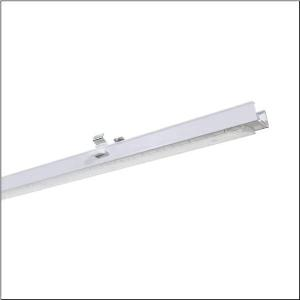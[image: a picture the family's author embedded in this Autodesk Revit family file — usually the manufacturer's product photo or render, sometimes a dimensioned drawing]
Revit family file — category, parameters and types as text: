
# Revit family: trunking_flex_31_51re14mb4cb
name_source: partatom
category: Lighting Fixtures
units: mm (PartAtom-declared; Revit-internal decimal feet)

## family parameters
Cut with Voids When Loaded = No
Host = Face
Light Source = No
Part Type = Normal
Room Calculation Point = No
Round Connector Dimension = Use Diameter
Shared = No

## types (1)
- --- (1 x LED, 11500 lm, 66 W, 4000K)
    Apparent Load = 66 VA
    CIE Flux Codes = 72 92 98 99 100
    Color Rendering = 80
    Color Temperature = 4000K
    Default Elevation = 1800 mm
    Description = Trunking Flex 31, luminaire insert, of extruded aluminium section, coated, traffic white (RAL 9016), length: 1.472mm, width: 91mm, height: 53mm, LED rated luminous flux: 11.500lm, light colour: 840, control gear: ON/OFF Multilumen, with system connector: socket, mains connection: 220..240V, AC, 50/60Hz, rated input power: 66W, connected load according to luminous flux setting (19/24/32/37/47/52/60/66W), luminous flux adjustable on luminaire in eight steps (3450/4380/5800/6700/8350/9200/10500/11500lm ), primary light control with lens, of plastic, primary optical cover: cover, of PMMA, light emission: direct distribution, primary light characteristic: asymmetric, protection rating (complete): IP20, insulation class (complete): insulation class I (protective earthing), certification: CE, UKCA, impact resistance: IK02, permissible ambient temperature for indoor applications: -20..+40°C, packaging unit: 1 piece
    Height = 58 mm
    Lamp = 1 x LED
    Lamp Light Flux = 11500 lm
    Lamp Power = 66 W
    Lamp count = 1
    Length = 1472 mm
    Luminous efficacy = 174 lm/W
    Manufacturer = Siteco
    ModVariant = No
    Model = 51RE14MB4CB
    Mounting Place = Ceiling
    Mounting Type = Pendant
    Number of Poles = 1
    OnlyDefault = Yes
    Power Factor = 1
    Product Name = Trunking Flex 31
    Product group = luminaire insert
    ProductGroupID = 901
    Protection Class = Protection class I
    Protection Degree = IP 20
    RLX_Detail_Level = 1
    RLX_Emergency_Light_Flux = 0 lm
    RLX_Emergency_Type = 0
    RLX_Emergency_Type_DB = No
    RlxData = <blob elided: 21737 chars, md5=bfbce8fc>
    Socket = socket
    Standby Power = 0 W
    System Light Flux = 11500 lm
    System Power = 66 W
    Type Comments = factory setting: luminous flux: 100 % | (ON | ON | ON)
    Type Image = l_1266702.jpg
    URL = http://relux.com
    VarID = @adj_018751
    Voltage = 0 V
    Weight = 0.00 kg
    Width = 65 mm

## geometry (parser evidence)
native form markers: Blend x4, Sweep x13
no freeform markers — native parametric forms only
